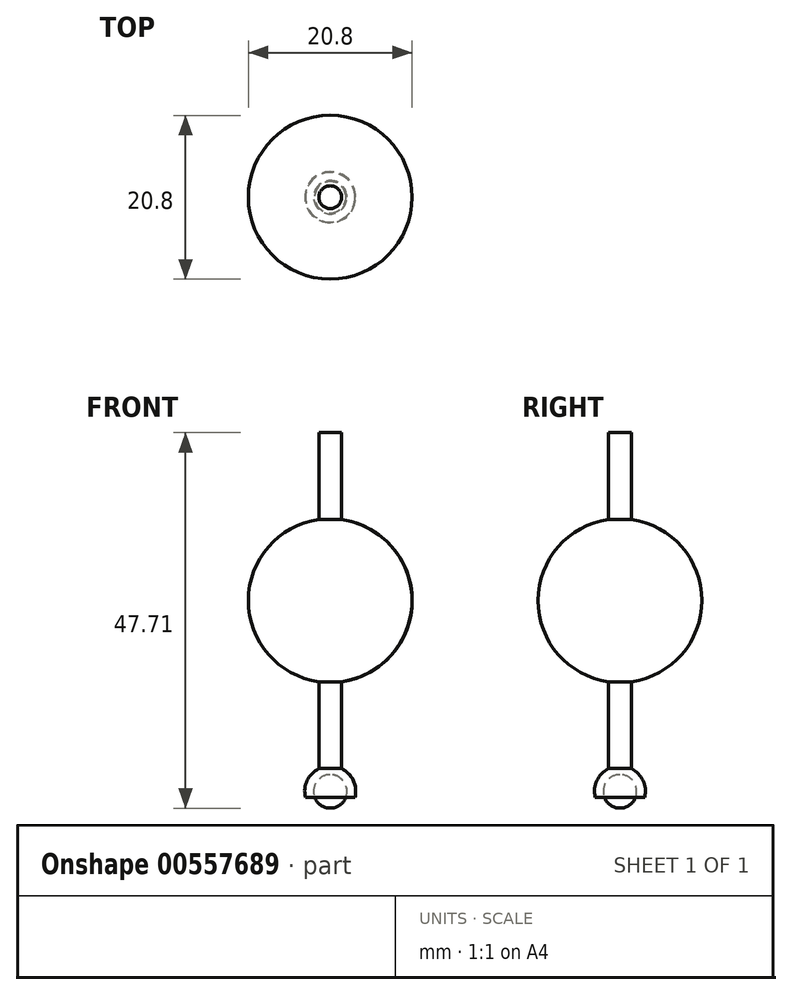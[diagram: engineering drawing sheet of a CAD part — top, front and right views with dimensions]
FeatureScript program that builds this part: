
annotation { "Feature Type Name" : "Feature", "Feature Type Description" : "" }
export const myFeature = defineFeature(function(context is Context, id is Id, definition is map)
    precondition{}
    {
        {
            var Q0;
            Q0=qCreatedBy(makeId("Front.planeOp"),FACE);
            var sketch = newSketch(context, id + "F0", { "sketchPlane" : qUnion([Q0])});
            skLineSegment(sketch, "E0", {"start": v(0, 33.72) * mm, "end": v(0, -8.97) * mm});
            skLineSegment(sketch, "E1", {"start": v(0, -8.97) * mm, "end": v(-1.45, -8.97) * mm});
            skLineSegment(sketch, "E2", {"start": v(-1.45, -8.97) * mm, "end": v(-1.45, 33.72) * mm});
            skLineSegment(sketch, "E3", {"start": v(-1.45, 33.72) * mm, "end": v(0, 33.72) * mm});
            skPoint(sketch, "E4", {"position": v(0, 12.38) * mm});
            skArc(sketch, "E5", {"start": v(0, 22.78) * mm, "mid": v(-10.4, 12.38) * mm, "end": v(0, 1.97) * mm});
            skArc(sketch, "E6", {"start": v(-1.45, -8.97) * mm, "mid": v(-3.15, -12.6) * mm, "end": v(0, -15.1) * mm});
            skLineSegment(sketch, "E7", {"start": v(0, -8.62) * mm, "end": v(0, -15.1) * mm});
            skLineSegment(sketch, "E8", {"start": v(-3.15, -12.6) * mm, "end": v(0, -12.6) * mm});
            skArc(sketch, "E9", {"start": v(0, -9.73) * mm, "mid": v(-2.13, -11.86) * mm, "end": v(0, -13.99) * mm});
            skLineSegment(sketch, "E10", {"start": v(0, -13.3) * mm, "end": v(-1.57, -13.3) * mm});
            skSolve(sketch);
        }
        {
            var Q0;
            {var subQ0=sQuery(id+"F0.wireOp",EDGE,"E5");var subQ1=sQuery(id+"F0.wireOp",EDGE,"E2");var subQ2=makeQuery(id+"F0.imprint","INTERSECT",VERTEX,{"disambiguationData":[OD(0.0)],"derivedFrom":[subQ1,subQ0]});Q0=makeQuery(id+"F0.imprint","IMPRINT",FACE,{"disambiguationData":[TD([[makeQuery(id+"F0.imprint","IMPRINT",EDGE,{"disambiguationData":[TD([[subQ2,-1.0]])],"derivedFrom":subQ1}),1.0]])]});}
            var Q1;
            {var subQ0=sQuery(id+"F0.wireOp",EDGE,"E5");var subQ1=sQuery(id+"F0.wireOp",EDGE,"E0");var subQ2=makeQuery(id+"F0.imprint","INTERSECT",VERTEX,{"disambiguationData":[OD(0.0)],"derivedFrom":[subQ1,subQ0]});Q1=makeQuery(id+"F0.imprint","IMPRINT",FACE,{"disambiguationData":[TD([[makeQuery(id+"F0.imprint","IMPRINT",EDGE,{"disambiguationData":[TD([[subQ2,-1.0]])],"derivedFrom":subQ1}),-1.0]])]});}
            var Q2;
            {var subQ0=sQuery(id+"F0.wireOp",EDGE,"E3");Q2=makeQuery(id+"F0.imprint","IMPRINT",FACE,{"disambiguationData":[TD([[makeQuery(id+"F0.imprint","IMPRINT",EDGE,{"derivedFrom":subQ0}),-1.0]])]});}
            var Q3;
            {var subQ0=sQuery(id+"F0.wireOp",EDGE,"E1");Q3=makeQuery(id+"F0.imprint","IMPRINT",FACE,{"disambiguationData":[TD([[makeQuery(id+"F0.imprint","IMPRINT",EDGE,{"derivedFrom":subQ0}),-1.0]])]});}
            var Q4;
            {var subQ6=sQuery(id+"F0.wireOp",EDGE,"E1");Q4=makeQuery(id+"F0.imprint","IMPRINT",FACE,{"disambiguationData":[TD([[makeQuery(id+"F0.imprint","IMPRINT",EDGE,{"derivedFrom":subQ6}),1.0]])]});}
            var Q5;
            Q5=sQuery(id+"F0.wireOp",EDGE,"E0");
            revolve(context, id + "F1", {"entities" : qUnion([Q0, Q1, Q2, Q3, Q4]), "axis" : qUnion([Q5]), "revolveType" : RevolveType.FULL});
        }
        {
            var Q0;
            {var subQ3=sQuery(id+"F0.wireOp",EDGE,"E10");Q0=makeQuery(id+"F0.imprint","IMPRINT",FACE,{"disambiguationData":[TD([[makeQuery(id+"F0.imprint","IMPRINT",EDGE,{"derivedFrom":subQ3}),-1.0]])]});}
            var Q1;
            {var subQ3=sQuery(id+"F0.wireOp",EDGE,"E10");Q1=makeQuery(id+"F0.imprint","IMPRINT",FACE,{"disambiguationData":[TD([[makeQuery(id+"F0.imprint","IMPRINT",EDGE,{"derivedFrom":subQ3}),1.0]])]});}
            var Q2;
            {var subQ0=sQuery(id+"F0.wireOp",EDGE,"E8");var subQ1=sQuery(id+"F0.wireOp",EDGE,"E7");var subQ2=makeQuery(id+"F0.imprint","INTERSECT",VERTEX,{"derivedFrom":[subQ1,subQ0]});Q2=makeQuery(id+"F0.imprint","IMPRINT",FACE,{"disambiguationData":[TD([[makeQuery(id+"F0.imprint","IMPRINT",EDGE,{"disambiguationData":[TD([[subQ2,1.0]])],"derivedFrom":subQ1}),-1.0]])]});}
            var Q3;
            Q3=sQuery(id+"F0.wireOp",EDGE,"E7");
            revolve(context, id + "F2", {"entities" : qUnion([Q0, Q1, Q2]), "axis" : qUnion([Q3]), "revolveType" : RevolveType.FULL});
        }
    });
